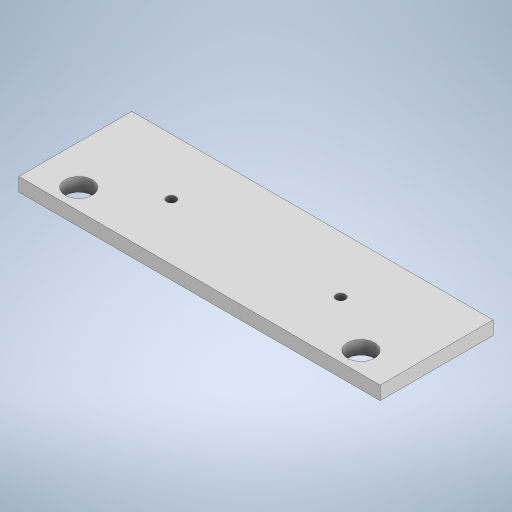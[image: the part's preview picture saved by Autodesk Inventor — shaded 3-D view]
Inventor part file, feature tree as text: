
AUTODESK INVENTOR PART (.ipt)
format: ipt  version: 2023.2 (Build 272271000, 271)  size: 240,640 bytes
history: native  units: mm
features: sketch x2, extrude x1, hole x1
ambient origin geometry x8: Origin, YZ Plane, XZ Plane, XY Plane, X Axis, Y Axis, Z Axis, Center Point
bodies: Solid1 (feature_tree)
feature tree (4):
  extrude  "Extrusion1"  Depth=50.0mm
  hole  "Hole1"  [1 undecoded]
  sketch  "Sketch1"  dims[d0=160.0mm d1=50.0mm]
  sketch  "Sketch2"  dims[d2=9.0mm d3=12.0mm d4=12.0mm d5=125.0mm d6=17.5mm d7=6.0mm d8=0.0mm d9=4.8mm d10=4.8mm d11=75.0mm d12=42.5mm d13=4.134mm d14=10.0mm d15=4.0mm d16=2.0mm d17=90.0deg d18=8.0mm d19=20.594885mm]
note: 1 required parameter value undecoded (feature->parameter linkage not recoverable at this tier; creation-order binding heuristic only, values carry confidence <= 0.55)
